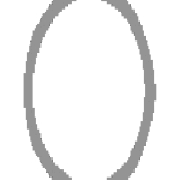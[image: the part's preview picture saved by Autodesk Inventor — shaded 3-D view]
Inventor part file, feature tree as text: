
AUTODESK INVENTOR PART (.ipt)
format: ipt  version: 2021 (Build 250183000, 183)  size: 110,080 bytes
history: native  units: in
note: dims shown in document units (in); Inventor stores cm internally (conversion verified against a paired STEP export)
features: other x4, sketch x3, plane x1
ambient origin geometry x8: Origin, YZ Plane, XZ Plane, XY Plane, X Axis, Y Axis, Z Axis, Center Point
bodies: Solid1 (feature_tree), Body (feature_tree)
feature tree (8):
  other  "Driven Length"
  other  "Frame Generator"
  other  "Start Plane"
  other  "End Plane"
  sketch  "Sketch"  dims[d2=9.0139in d4=-0.0in d5=9.0139in d6=0.12in d7=0.0in d8=90.0deg d9=9.0139in]
  sketch  "Sketch2"  dims[d0=1.0in]
  plane  "Work Plane3"
  sketch  "Sketch3"  dims[d1=0.065in]
